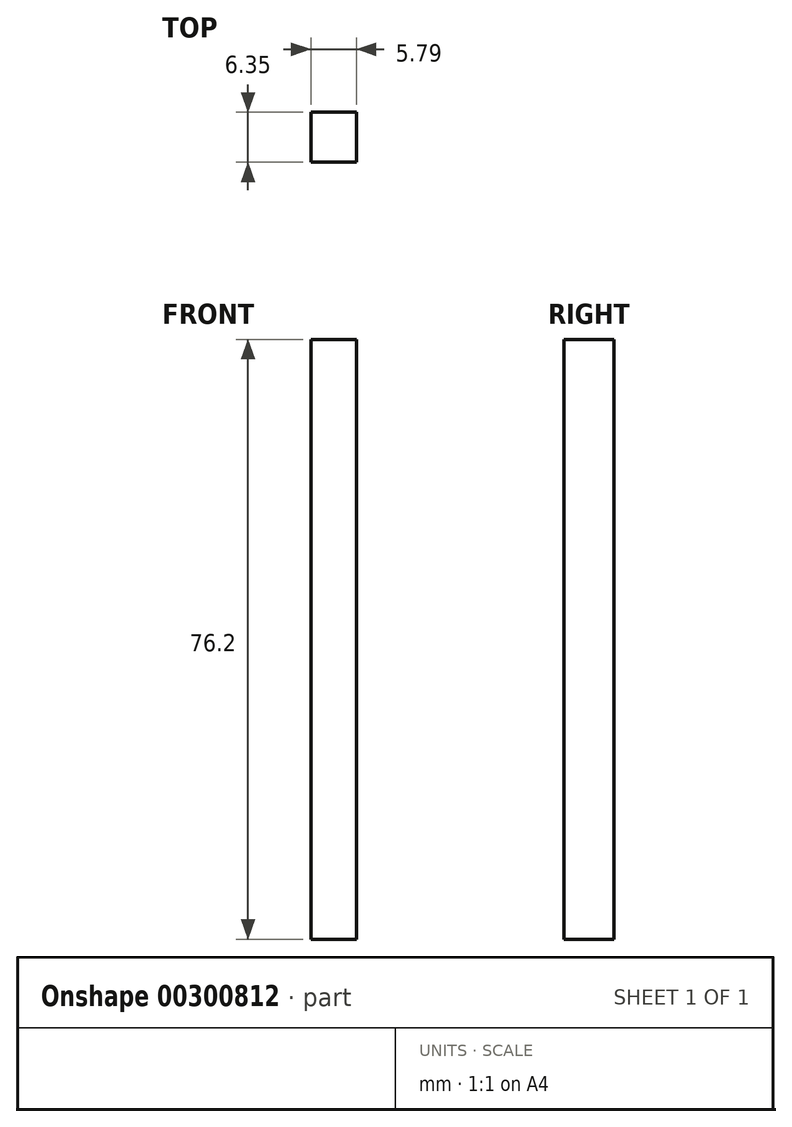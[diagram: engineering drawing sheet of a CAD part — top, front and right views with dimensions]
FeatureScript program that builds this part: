
annotation { "Feature Type Name" : "Feature", "Feature Type Description" : "" }
export const myFeature = defineFeature(function(context is Context, id is Id, definition is map)
    precondition{}
    {
        {
            var Q0;
            Q0=qCreatedBy(makeId("Front.planeOp"),FACE);
            var sketch = newSketch(context, id + "F0", { "sketchPlane" : qUnion([Q0])});
            skLineSegment(sketch, "E0.bottom", {"start": v(-23.67, 106.3) * mm, "end": v(-17.88, 106.3) * mm});
            skLineSegment(sketch, "E0.top", {"start": v(-23.67, 30.1) * mm, "end": v(-17.88, 30.1) * mm});
            skLineSegment(sketch, "E0.left", {"start": v(-23.67, 106.3) * mm, "end": v(-23.67, 30.1) * mm});
            skLineSegment(sketch, "E0.right", {"start": v(-17.88, 106.3) * mm, "end": v(-17.88, 30.1) * mm});
            skSolve(sketch);
        }
        {
            var Q0;
            Q0 = qSketchRegion(id + "F0", true);
            extrude(context, id + "F1", {"entities" : qUnion([Q0]), "depth" : 6.35 * mm});
        }
    });
